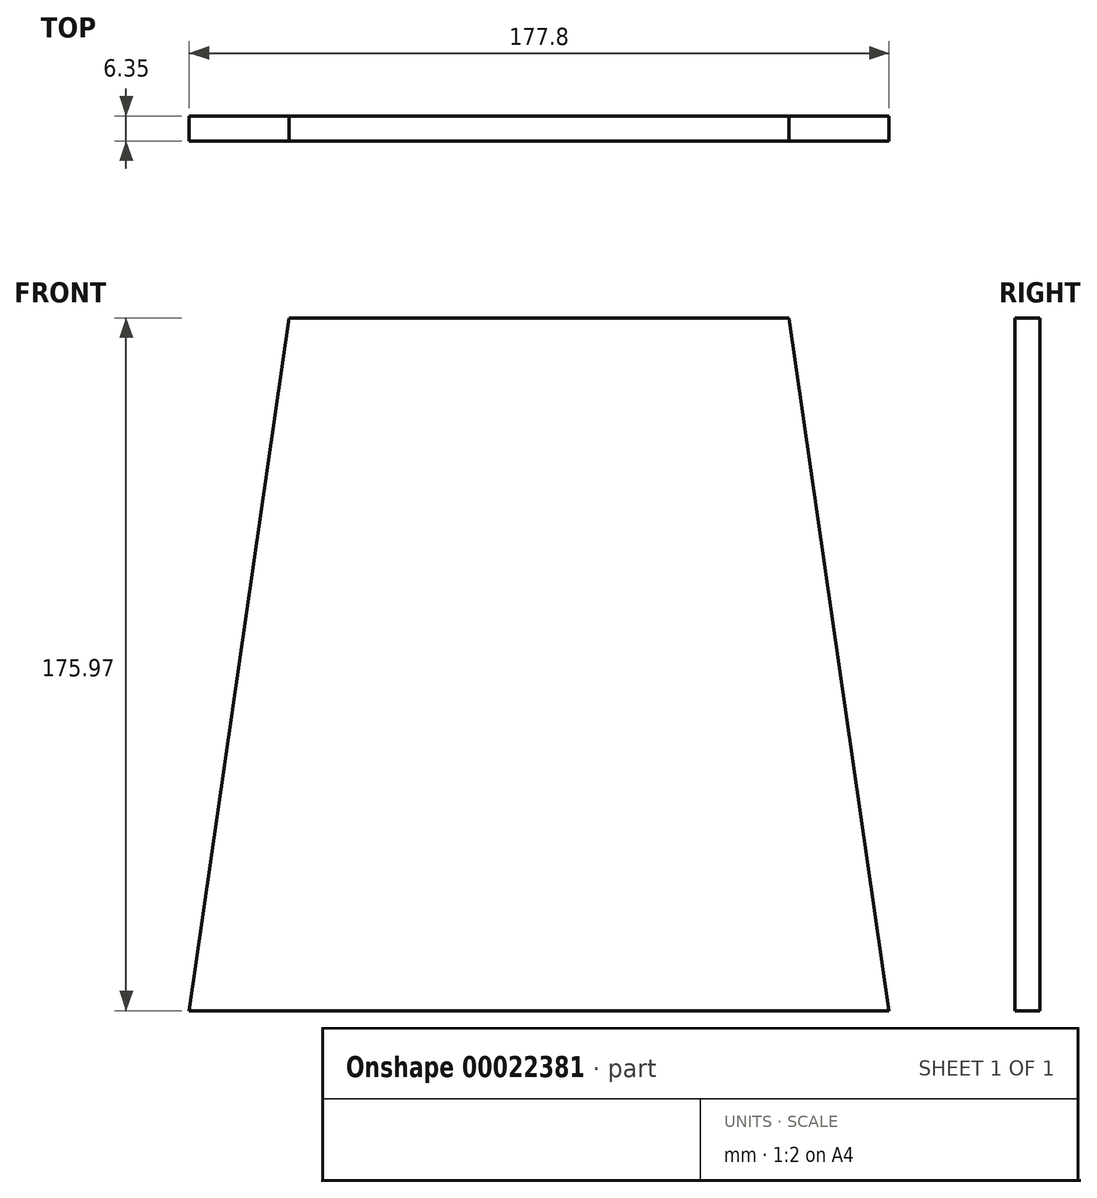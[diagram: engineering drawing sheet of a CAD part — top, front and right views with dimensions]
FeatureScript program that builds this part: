
annotation { "Feature Type Name" : "Feature", "Feature Type Description" : "" }
export const myFeature = defineFeature(function(context is Context, id is Id, definition is map)
    precondition{}
    {
        {
            var Q0;
            Q0=qCreatedBy(makeId("Front.planeOp"),FACE);
            var sketch = newSketch(context, id + "F0", { "sketchPlane" : qUnion([Q0])});
            skLineSegment(sketch, "E0", {"start": v(-130.96, 13.78) * mm, "end": v(-156.36, -162.2) * mm});
            skLineSegment(sketch, "E1.bottom", {"start": v(-130.96, 13.78) * mm, "end": v(-3.96, 13.78) * mm});
            skLineSegment(sketch, "E1.top", {"start": v(-132.07, -162.2) * mm, "end": v(0, -162.2) * mm});
            skLineSegment(sketch, "E2", {"start": v(-156.36, -162.2) * mm, "end": v(21.44, -162.2) * mm});
            skLineSegment(sketch, "E3", {"start": v(-3.96, 13.78) * mm, "end": v(21.44, -162.2) * mm});
            skSolve(sketch);
        }
        {
            var Q0;
            {var subQ2=sQuery(id+"F0.wireOp",EDGE,"E0");Q0=makeQuery(id+"F0.imprint","IMPRINT",FACE,{"disambiguationData":[TD([[makeQuery(id+"F0.imprint","IMPRINT",EDGE,{"derivedFrom":subQ2}),1.0]])]});}
            extrude(context, id + "F1", {"entities" : qUnion([Q0]), "depth" : 6.35 * mm});
        }
    });
